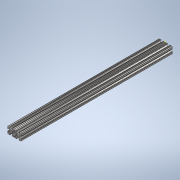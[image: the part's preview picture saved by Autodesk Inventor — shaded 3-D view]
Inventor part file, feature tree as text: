
AUTODESK INVENTOR PART (.ipt)
format: ipt  version: 2020 (Build 240168000, 168)  size: 353,792 bytes
history: native  units: in
note: dims shown in document units (in); Inventor stores cm internally (conversion verified against a paired STEP export)
features: sketch x2, extrude x1
ambient origin geometry x8: Origin, YZ Plane, XZ Plane, XY Plane, X Axis, Y Axis, Z Axis, Center Point
bodies: Solid1 (feature_tree)
feature tree (3):
  extrude  "Extrusion1"  [1 undecoded]
  sketch  "Sketch2"
  sketch  "Sketch1"  dims[d0=22.0in d1=0.0in]
note: 1 required parameter value undecoded (feature->parameter linkage not recoverable at this tier; creation-order binding heuristic only, values carry confidence <= 0.55)
